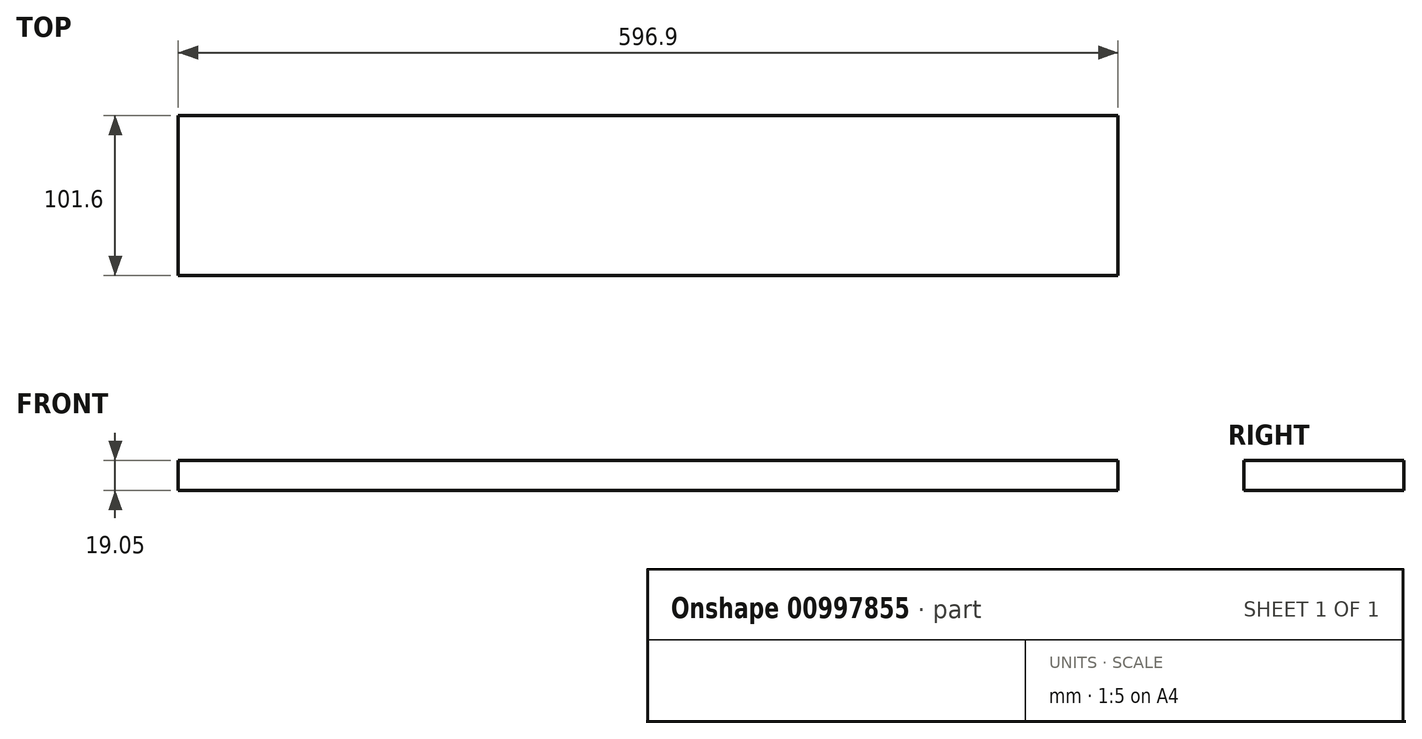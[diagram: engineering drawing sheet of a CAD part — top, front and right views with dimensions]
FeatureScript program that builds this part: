
annotation { "Feature Type Name" : "Feature", "Feature Type Description" : "" }
export const myFeature = defineFeature(function(context is Context, id is Id, definition is map)
    precondition{}
    {
        {
            var Q0;
            Q0=qCreatedBy(makeId("Top.planeOp"),FACE);
            var sketch = newSketch(context, id + "F0", { "sketchPlane" : qUnion([Q0])});
            skLineSegment(sketch, "E0.bottom", {"start": v(298.45, -50.8) * mm, "end": v(-298.45, -50.8) * mm});
            skLineSegment(sketch, "E0.top", {"start": v(298.45, 50.8) * mm, "end": v(-298.45, 50.8) * mm});
            skLineSegment(sketch, "E0.left", {"start": v(298.45, -50.8) * mm, "end": v(298.45, 50.8) * mm});
            skLineSegment(sketch, "E0.right", {"start": v(-298.45, -50.8) * mm, "end": v(-298.45, 50.8) * mm});
            skPoint(sketch, "E0.middle", {"position": v(0, 0) * mm});
            skSolve(sketch);
        }
        {
            var Q0;
            Q0=makeQuery(id+"F0.imprint","IMPRINT",FACE,{"disambiguationData":[TD([[makeQuery(id+"F0.imprint","IMPRINT",EDGE,{"derivedFrom":sQuery(id+"F0.wireOp",EDGE,"E0.bottom")}),-1.0]])]});
            extrude(context, id + "F1", {"entities" : qUnion([Q0]), "depth" : 19.05 * mm, "offsetDistance" : 25.4 * mm});
        }
    });
